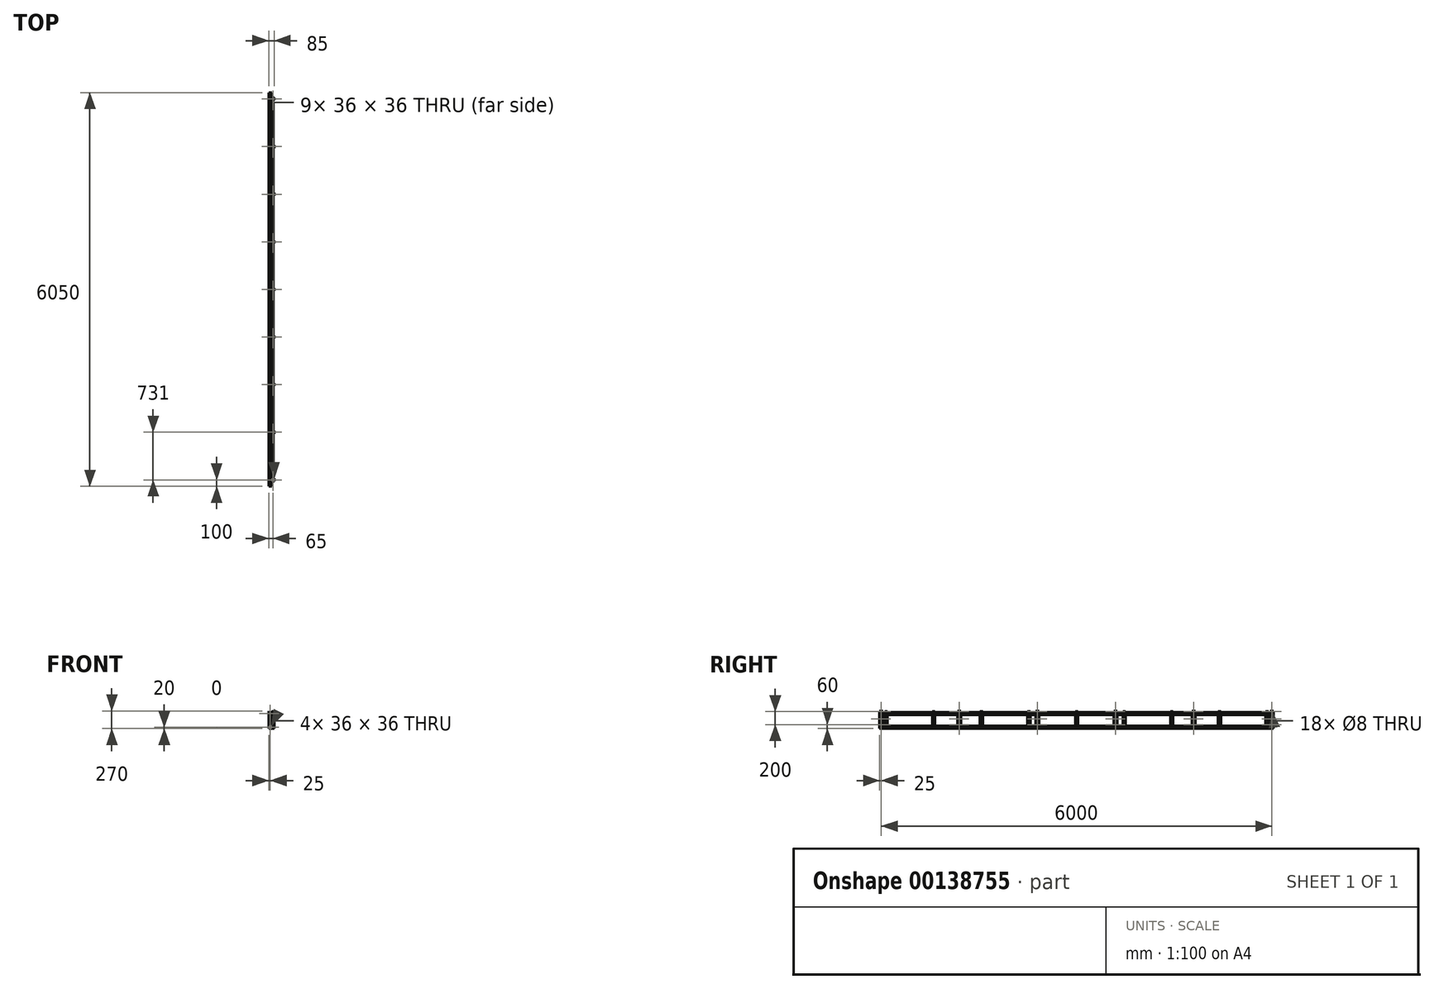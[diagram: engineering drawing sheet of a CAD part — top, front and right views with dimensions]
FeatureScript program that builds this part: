
annotation { "Feature Type Name" : "Feature", "Feature Type Description" : "" }
export const myFeature = defineFeature(function(context is Context, id is Id, definition is map)
    precondition{}
    {
        {
            var Q0;
            Q0=qCreatedBy(makeId("Front.planeOp"),FACE);
            var sketch = newSketch(context, id + "F0", { "sketchPlane" : qUnion([Q0])});
            skLineSegment(sketch, "E0.bottom", {"start": v(0, 85) * mm, "end": v(40, 85) * mm});
            skLineSegment(sketch, "E0.top", {"start": v(0, 125) * mm, "end": v(40, 125) * mm});
            skLineSegment(sketch, "E0.left", {"start": v(0, 85) * mm, "end": v(0, 125) * mm});
            skLineSegment(sketch, "E0.right", {"start": v(40, 85) * mm, "end": v(40, 125) * mm});
            skLineSegment(sketch, "E1.bottom", {"start": v(0, -85) * mm, "end": v(40, -85) * mm});
            skLineSegment(sketch, "E1.top", {"start": v(0, -125) * mm, "end": v(40, -125) * mm});
            skLineSegment(sketch, "E1.left", {"start": v(0, -85) * mm, "end": v(0, -125) * mm});
            skLineSegment(sketch, "E1.right", {"start": v(40, -85) * mm, "end": v(40, -125) * mm});
            skSolve(sketch);
        }
        {
            var Q0;
            Q0=qSketchRegion(id+"F0",true);
            extrude(context, id + "F1", {"entities" : qUnion([Q0]), "oppositeDirection" : true, "depth" : 3025 * mm});
        }
        {
            var Q0;
            Q0=makeQuery(id+"F1.opExtrude","CAP_FACE",FACE,{"disambiguationData":[OSD([sQuery(id+"F0.wireOp",EDGE,"E0.bottom"),sQuery(id+"F0.wireOp",EDGE,"E0.top"),sQuery(id+"F0.wireOp",EDGE,"E0.left"),sQuery(id+"F0.wireOp",EDGE,"E0.right")])],"isStart":true});
            var Q1;
            Q1=makeQuery(id+"F1.opExtrude","CAP_FACE",FACE,{"disambiguationData":[OSD([sQuery(id+"F0.wireOp",EDGE,"E1.bottom"),sQuery(id+"F0.wireOp",EDGE,"E1.top"),sQuery(id+"F0.wireOp",EDGE,"E1.left"),sQuery(id+"F0.wireOp",EDGE,"E1.right")])],"isStart":true});
            var Q2;
            Q2=makeQuery(id+"F1.opExtrude","CAP_FACE",FACE,{"disambiguationData":[OSD([sQuery(id+"F0.wireOp",EDGE,"E0.bottom"),sQuery(id+"F0.wireOp",EDGE,"E0.top"),sQuery(id+"F0.wireOp",EDGE,"E0.left"),sQuery(id+"F0.wireOp",EDGE,"E0.right")])],"isStart":false});
            var Q3;
            Q3=makeQuery(id+"F1.opExtrude","CAP_FACE",FACE,{"disambiguationData":[OSD([sQuery(id+"F0.wireOp",EDGE,"E1.bottom"),sQuery(id+"F0.wireOp",EDGE,"E1.top"),sQuery(id+"F0.wireOp",EDGE,"E1.left"),sQuery(id+"F0.wireOp",EDGE,"E1.right")])],"isStart":false});
            shell(context, id + "F2", {"entities" : qUnion([Q0, Q1, Q2, Q3]), "thickness" : 2 * mm});
        }
        {
            var Q0;
            Q0=qCreatedBy(makeId("Right.planeOp"),FACE);
            var sketch = newSketch(context, id + "F3", { "sketchPlane" : qUnion([Q0])});
            skLineSegment(sketch, "E2", {"start": v(600, 417.5) * mm, "end": v(600, -382.26) * mm, "construction": true});
            skLineSegment(sketch, "E3", {"start": v(1800, -382.26) * mm, "end": v(1800, 527.08) * mm, "construction": true});
            skLineSegment(sketch, "E4", {"start": v(3000, 527.08) * mm, "end": v(3000, -411.1) * mm, "construction": true});
            skLineSegment(sketch, "E5.bottom", {"start": v(575, -125) * mm, "end": v(625, -125) * mm});
            skLineSegment(sketch, "E5.top", {"start": v(575, 145) * mm, "end": v(625, 145) * mm});
            skLineSegment(sketch, "E5.left", {"start": v(575, -125) * mm, "end": v(575, 145) * mm});
            skLineSegment(sketch, "E5.right", {"start": v(625, -125) * mm, "end": v(625, 145) * mm});
            skCircle(sketch, "E6", {"center": v(600, 135) * mm, "radius": 4 * mm});
            skCircle(sketch, "E7", {"center": v(600, 25) * mm, "radius": 4 * mm});
            skCircle(sketch, "E8", {"center": v(600, -65) * mm, "radius": 4 * mm});
            skLineSegment(sketch, "E9.1.0.0", {"start": v(1775, 145) * mm, "end": v(1825, 145) * mm});
            skCircle(sketch, "E9.1.0.1", {"center": v(1800, 135) * mm, "radius": 4 * mm});
            skLineSegment(sketch, "E9.1.0.2", {"start": v(1825, -125) * mm, "end": v(1825, 145) * mm});
            skLineSegment(sketch, "E9.1.0.3", {"start": v(1775, -125) * mm, "end": v(1775, 145) * mm});
            skCircle(sketch, "E9.1.0.4", {"center": v(1800, 25) * mm, "radius": 4 * mm});
            skLineSegment(sketch, "E9.1.0.5", {"start": v(1775, -125) * mm, "end": v(1825, -125) * mm});
            skCircle(sketch, "E9.1.0.6", {"center": v(1800, -65) * mm, "radius": 4 * mm});
            skLineSegment(sketch, "E9.2.0.0", {"start": v(2975, 145) * mm, "end": v(3025, 145) * mm});
            skCircle(sketch, "E9.2.0.1", {"center": v(3000, 135) * mm, "radius": 4 * mm});
            skLineSegment(sketch, "E9.2.0.2", {"start": v(3025, -125) * mm, "end": v(3025, 145) * mm});
            skLineSegment(sketch, "E9.2.0.3", {"start": v(2975, -125) * mm, "end": v(2975, 145) * mm});
            skCircle(sketch, "E9.2.0.4", {"center": v(3000, 25) * mm, "radius": 4 * mm});
            skLineSegment(sketch, "E9.2.0.5", {"start": v(2975, -125) * mm, "end": v(3025, -125) * mm});
            skCircle(sketch, "E9.2.0.6", {"center": v(3000, -65) * mm, "radius": 4 * mm});
            skLineSegment(sketch, "E9.direction1", {"start": v(625, 145) * mm, "end": v(1825, 145) * mm, "construction": true});
            skSolve(sketch);
        }
        {
            var Q0;
            Q0=qSketchRegion(id+"F3",true);
            extrude(context, id + "F4", {"entities" : qUnion([Q0]), "oppositeDirection" : true, "depth" : 5 * mm});
        }
        {
            var Q0;
            Q0=qCreatedBy(makeId("Top.planeOp"),FACE);
            var sketch = newSketch(context, id + "F5", { "sketchPlane" : qUnion([Q0])});
            skLineSegment(sketch, "E10.bottom", {"start": v(40, 2945) * mm, "end": v(80, 2945) * mm});
            skLineSegment(sketch, "E10.top", {"start": v(40, 2905) * mm, "end": v(80, 2905) * mm});
            skLineSegment(sketch, "E10.left", {"start": v(40, 2945) * mm, "end": v(40, 2905) * mm});
            skLineSegment(sketch, "E10.right", {"start": v(80, 2945) * mm, "end": v(80, 2905) * mm});
            skLineSegment(sketch, "E11.bottom", {"start": v(42, 2943) * mm, "end": v(78, 2943) * mm});
            skLineSegment(sketch, "E11.top", {"start": v(42, 2907) * mm, "end": v(78, 2907) * mm});
            skLineSegment(sketch, "E11.left", {"start": v(42, 2943) * mm, "end": v(42, 2907) * mm});
            skLineSegment(sketch, "E11.right", {"start": v(78, 2943) * mm, "end": v(78, 2907) * mm});
            skLineSegment(sketch, "E12.0.1.0", {"start": v(40, 2214) * mm, "end": v(80, 2214) * mm});
            skLineSegment(sketch, "E12.0.1.1", {"start": v(42, 2212) * mm, "end": v(78, 2212) * mm});
            skLineSegment(sketch, "E12.0.1.2", {"start": v(42, 2212) * mm, "end": v(42, 2176) * mm});
            skLineSegment(sketch, "E12.0.1.3", {"start": v(40, 2214) * mm, "end": v(40, 2174) * mm});
            skLineSegment(sketch, "E12.0.1.4", {"start": v(40, 2174) * mm, "end": v(80, 2174) * mm});
            skLineSegment(sketch, "E12.0.1.5", {"start": v(42, 2176) * mm, "end": v(78, 2176) * mm});
            skLineSegment(sketch, "E12.0.1.6", {"start": v(78, 2212) * mm, "end": v(78, 2176) * mm});
            skLineSegment(sketch, "E12.0.1.7", {"start": v(80, 2214) * mm, "end": v(80, 2174) * mm});
            skLineSegment(sketch, "E12.0.2.0", {"start": v(40, 1483) * mm, "end": v(80, 1483) * mm});
            skLineSegment(sketch, "E12.0.2.1", {"start": v(42, 1481) * mm, "end": v(78, 1481) * mm});
            skLineSegment(sketch, "E12.0.2.2", {"start": v(42, 1481) * mm, "end": v(42, 1445) * mm});
            skLineSegment(sketch, "E12.0.2.3", {"start": v(40, 1483) * mm, "end": v(40, 1443) * mm});
            skLineSegment(sketch, "E12.0.2.4", {"start": v(40, 1443) * mm, "end": v(80, 1443) * mm});
            skLineSegment(sketch, "E12.0.2.5", {"start": v(42, 1445) * mm, "end": v(78, 1445) * mm});
            skLineSegment(sketch, "E12.0.2.6", {"start": v(78, 1481) * mm, "end": v(78, 1445) * mm});
            skLineSegment(sketch, "E12.0.2.7", {"start": v(80, 1483) * mm, "end": v(80, 1443) * mm});
            skLineSegment(sketch, "E12.0.3.0", {"start": v(40, 752) * mm, "end": v(80, 752) * mm});
            skLineSegment(sketch, "E12.0.3.1", {"start": v(42, 750) * mm, "end": v(78, 750) * mm});
            skLineSegment(sketch, "E12.0.3.2", {"start": v(42, 750) * mm, "end": v(42, 714) * mm});
            skLineSegment(sketch, "E12.0.3.3", {"start": v(40, 752) * mm, "end": v(40, 712) * mm});
            skLineSegment(sketch, "E12.0.3.4", {"start": v(40, 712) * mm, "end": v(80, 712) * mm});
            skLineSegment(sketch, "E12.0.3.5", {"start": v(42, 714) * mm, "end": v(78, 714) * mm});
            skLineSegment(sketch, "E12.0.3.6", {"start": v(78, 750) * mm, "end": v(78, 714) * mm});
            skLineSegment(sketch, "E12.0.3.7", {"start": v(80, 752) * mm, "end": v(80, 712) * mm});
            skLineSegment(sketch, "E12.0.4.0", {"start": v(40, 21) * mm, "end": v(80, 21) * mm});
            skLineSegment(sketch, "E12.0.4.1", {"start": v(42, 19) * mm, "end": v(78, 19) * mm});
            skLineSegment(sketch, "E12.0.4.2", {"start": v(42, 19) * mm, "end": v(42, -17) * mm});
            skLineSegment(sketch, "E12.0.4.3", {"start": v(40, 21) * mm, "end": v(40, -19) * mm});
            skLineSegment(sketch, "E12.0.4.4", {"start": v(40, -19) * mm, "end": v(80, -19) * mm});
            skLineSegment(sketch, "E12.0.4.5", {"start": v(42, -17) * mm, "end": v(78, -17) * mm});
            skLineSegment(sketch, "E12.0.4.6", {"start": v(78, 19) * mm, "end": v(78, -17) * mm});
            skLineSegment(sketch, "E12.0.4.7", {"start": v(80, 21) * mm, "end": v(80, -19) * mm});
            skLineSegment(sketch, "E12.direction1", {"start": v(40, 2945) * mm, "end": v(65, 2945) * mm, "construction": true});
            skLineSegment(sketch, "E12.direction2", {"start": v(40, 2945) * mm, "end": v(40, 2214) * mm, "construction": true});
            skSolve(sketch);
        }
        {
            var Q0;
            Q0=qSketchRegion(id+"F5",true);
            extrude(context, id + "F6", {"entities" : qUnion([Q0]), "depth" : 135 * mm, "hasSecondDirection" : true, "secondDirectionOppositeDirection" : true, "secondDirectionDepth" : 125 * mm});
        }
        {
            var Q0;
            Q0=makeQuery(id+"F1.opExtrude","SWEPT_BODY",BODY,{"disambiguationData":[OSD([sQuery(id+"F0.wireOp",EDGE,"E0.bottom"),sQuery(id+"F0.wireOp",EDGE,"E0.top"),sQuery(id+"F0.wireOp",EDGE,"E0.left"),sQuery(id+"F0.wireOp",EDGE,"E0.right")])]});
            var Q1;
            Q1=makeQuery(id+"F1.opExtrude","SWEPT_BODY",BODY,{"disambiguationData":[OSD([sQuery(id+"F0.wireOp",EDGE,"E1.bottom"),sQuery(id+"F0.wireOp",EDGE,"E1.top"),sQuery(id+"F0.wireOp",EDGE,"E1.left"),sQuery(id+"F0.wireOp",EDGE,"E1.right")])]});
            var Q2;
            Q2=makeQuery(id+"F4.opExtrude","SWEPT_BODY",BODY,{"disambiguationData":[OSD([sQuery(id+"F3.wireOp",EDGE,"E5.bottom"),sQuery(id+"F3.wireOp",EDGE,"E5.top"),sQuery(id+"F3.wireOp",EDGE,"E5.left"),sQuery(id+"F3.wireOp",EDGE,"E5.right"),sQuery(id+"F3.wireOp",EDGE,"E6"),sQuery(id+"F3.wireOp",EDGE,"E7"),sQuery(id+"F3.wireOp",EDGE,"E8")])]});
            var Q3;
            Q3=makeQuery(id+"F6.opExtrude","SWEPT_BODY",BODY,{"disambiguationData":[OSD([sQuery(id+"F5.wireOp",EDGE,"E12.0.3.0"),sQuery(id+"F5.wireOp",EDGE,"E12.0.3.1"),sQuery(id+"F5.wireOp",EDGE,"E12.0.3.2"),sQuery(id+"F5.wireOp",EDGE,"E12.0.3.3"),sQuery(id+"F5.wireOp",EDGE,"E12.0.3.4"),sQuery(id+"F5.wireOp",EDGE,"E12.0.3.5"),sQuery(id+"F5.wireOp",EDGE,"E12.0.3.6"),sQuery(id+"F5.wireOp",EDGE,"E12.0.3.7")])]});
            var Q4;
            Q4=makeQuery(id+"F4.opExtrude","SWEPT_BODY",BODY,{"disambiguationData":[OSD([sQuery(id+"F3.wireOp",EDGE,"E9.2.0.0"),sQuery(id+"F3.wireOp",EDGE,"E9.2.0.1"),sQuery(id+"F3.wireOp",EDGE,"E9.2.0.2"),sQuery(id+"F3.wireOp",EDGE,"E9.2.0.3"),sQuery(id+"F3.wireOp",EDGE,"E9.2.0.4"),sQuery(id+"F3.wireOp",EDGE,"E9.2.0.5"),sQuery(id+"F3.wireOp",EDGE,"E9.2.0.6")])]});
            var Q5;
            Q5=makeQuery(id+"F6.opExtrude","SWEPT_BODY",BODY,{"disambiguationData":[OSD([sQuery(id+"F5.wireOp",EDGE,"E10.bottom"),sQuery(id+"F5.wireOp",EDGE,"E10.top"),sQuery(id+"F5.wireOp",EDGE,"E10.left"),sQuery(id+"F5.wireOp",EDGE,"E10.right"),sQuery(id+"F5.wireOp",EDGE,"E11.bottom"),sQuery(id+"F5.wireOp",EDGE,"E11.top"),sQuery(id+"F5.wireOp",EDGE,"E11.left"),sQuery(id+"F5.wireOp",EDGE,"E11.right")])]});
            var Q6;
            Q6=makeQuery(id+"F6.opExtrude","SWEPT_BODY",BODY,{"disambiguationData":[OSD([sQuery(id+"F5.wireOp",EDGE,"E12.0.1.0"),sQuery(id+"F5.wireOp",EDGE,"E12.0.1.1"),sQuery(id+"F5.wireOp",EDGE,"E12.0.1.2"),sQuery(id+"F5.wireOp",EDGE,"E12.0.1.3"),sQuery(id+"F5.wireOp",EDGE,"E12.0.1.4"),sQuery(id+"F5.wireOp",EDGE,"E12.0.1.5"),sQuery(id+"F5.wireOp",EDGE,"E12.0.1.6"),sQuery(id+"F5.wireOp",EDGE,"E12.0.1.7")])]});
            var Q7;
            Q7=makeQuery(id+"F4.opExtrude","SWEPT_BODY",BODY,{"disambiguationData":[OSD([sQuery(id+"F3.wireOp",EDGE,"E9.1.0.0"),sQuery(id+"F3.wireOp",EDGE,"E9.1.0.1"),sQuery(id+"F3.wireOp",EDGE,"E9.1.0.2"),sQuery(id+"F3.wireOp",EDGE,"E9.1.0.3"),sQuery(id+"F3.wireOp",EDGE,"E9.1.0.4"),sQuery(id+"F3.wireOp",EDGE,"E9.1.0.5"),sQuery(id+"F3.wireOp",EDGE,"E9.1.0.6")])]});
            var Q8;
            Q8=makeQuery(id+"F6.opExtrude","SWEPT_BODY",BODY,{"disambiguationData":[OSD([sQuery(id+"F5.wireOp",EDGE,"E12.0.2.0"),sQuery(id+"F5.wireOp",EDGE,"E12.0.2.1"),sQuery(id+"F5.wireOp",EDGE,"E12.0.2.2"),sQuery(id+"F5.wireOp",EDGE,"E12.0.2.3"),sQuery(id+"F5.wireOp",EDGE,"E12.0.2.4"),sQuery(id+"F5.wireOp",EDGE,"E12.0.2.5"),sQuery(id+"F5.wireOp",EDGE,"E12.0.2.6"),sQuery(id+"F5.wireOp",EDGE,"E12.0.2.7")])]});
            var Q9;
            Q9=qCreatedBy(makeId("Front.planeOp"),FACE);
            mirror(context, id + "F7", {"entities" : qUnion([Q0, Q1, Q2, Q3, Q4, Q5, Q6, Q7, Q8]), "mirrorPlane" : qUnion([Q9])});
        }
    });
